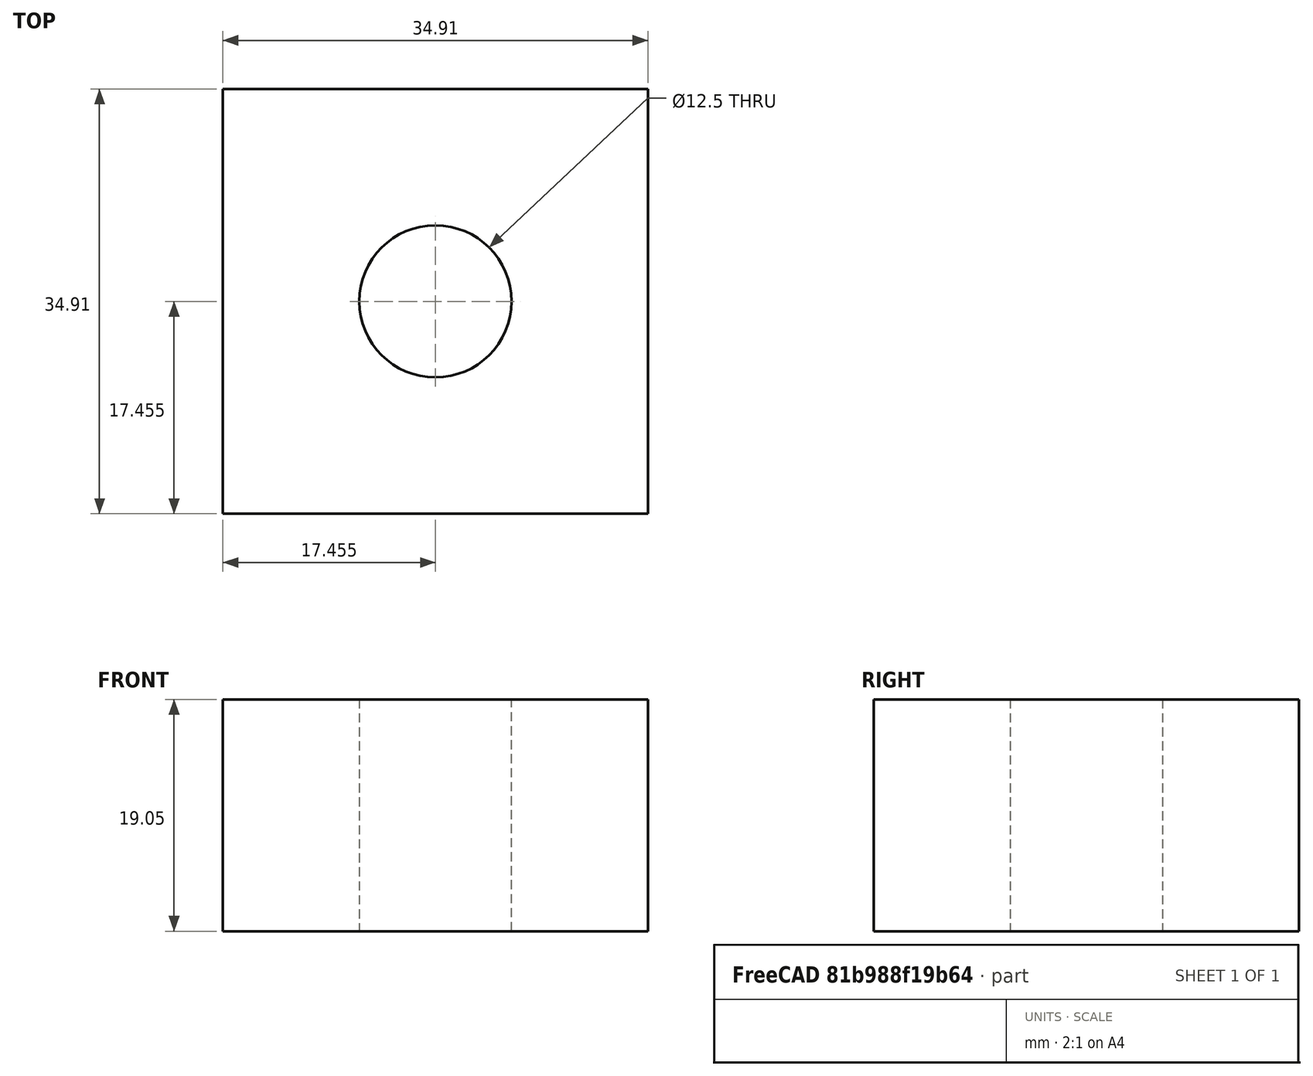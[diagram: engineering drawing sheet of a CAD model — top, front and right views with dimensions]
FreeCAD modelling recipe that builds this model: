
FCSTD DOCUMENT  (FreeCAD 0.19R24291 (Git))
Label: footMountFront
License: All rights reserved
LicenseURL: http://en.wikipedia.org/wiki/All_rights_reserved
objects: Sketcher::SketchObject×1, PartDesign::Pad×1, PartDesign::Body×1
note: 4 computed .brp shape members not serialized (recipe doc carries the construction recipe); baked Part::Feature solids carry a one-line shape summary decoded from their .brp

FEATURE [Sketcher::SketchObject] Sketch
  FullyConstrained = false
  MapMode = 5
  Support = -> [XY_Plane]
  sketch-geometry (24):
    g0: LineSegment StartX=0 StartY=562.08 StartZ=0 EndX=19.08 EndY=562.08 EndZ=0
    g1: LineSegment StartX=19.08 StartY=562.08 StartZ=0 EndX=19.08 EndY=19.08 EndZ=0
    g2: LineSegment StartX=19.08 StartY=19.08 StartZ=0 EndX=0 EndY=19.08 EndZ=0
    g3: LineSegment StartX=0 StartY=19.08 StartZ=0 EndX=0 EndY=562.08 EndZ=0
    g4: LineSegment StartX=0 StartY=0 StartZ=0 EndX=647.65 EndY=0 EndZ=0
    g5: LineSegment StartX=647.65 StartY=0 StartZ=0 EndX=647.65 EndY=19.08 EndZ=0
    g6: LineSegment StartX=647.65 StartY=19.08 StartZ=0 EndX=0 EndY=19.08 EndZ=0
    g7: LineSegment StartX=0 StartY=19.08 StartZ=0 EndX=0 EndY=0 EndZ=0
    g8: LineSegment StartX=628.57 StartY=562.08 StartZ=0 EndX=647.65 EndY=562.08 EndZ=0
    g9: LineSegment StartX=647.65 StartY=562.08 StartZ=0 EndX=647.65 EndY=19.08 EndZ=0
    g10: LineSegment StartX=647.65 StartY=19.08 StartZ=0 EndX=628.57 EndY=19.08 EndZ=0
    g11: LineSegment StartX=628.57 StartY=19.08 StartZ=0 EndX=628.57 EndY=562.08 EndZ=0
    g12: LineSegment StartX=19.08 StartY=19.08 StartZ=0 EndX=53.99 EndY=19.08 EndZ=0
    g13: LineSegment StartX=53.99 StartY=19.08 StartZ=0 EndX=53.99 EndY=53.99 EndZ=0
    g14: LineSegment StartX=53.99 StartY=53.99 StartZ=0 EndX=19.08 EndY=53.99 EndZ=0
    g15: LineSegment StartX=19.08 StartY=53.99 StartZ=0 EndX=19.08 EndY=19.08 EndZ=0
    g16: LineSegment StartX=-141.684 StartY=53.99 StartZ=0 EndX=670.005 EndY=53.99 EndZ=0
    g17: LineSegment StartX=670.005 StartY=53.99 StartZ=0 EndX=670.005 EndY=-34.91 EndZ=0
    g18: LineSegment StartX=670.005 StartY=-34.91 StartZ=0 EndX=-141.684 EndY=-34.91 EndZ=0
    g19: LineSegment StartX=-141.684 StartY=-34.91 StartZ=0 EndX=-141.684 EndY=53.99 EndZ=0
    g20: LineSegment StartX=-141.684 StartY=9.54 StartZ=0 EndX=0 EndY=9.54 EndZ=0
    g21: LineSegment StartX=19.08 StartY=53.99 StartZ=0 EndX=53.99 EndY=19.08 EndZ=0
    g22: LineSegment StartX=53.99 StartY=53.99 StartZ=0 EndX=19.08 EndY=19.08 EndZ=0
    g23: Circle CenterX=36.535 CenterY=36.535 CenterZ=0 NormalX=0 NormalY=0 NormalZ=1 AngleXU=0 Radius=6.25
  constraints (64):
    c: Coincident(g0,g1)
    c: Coincident(g1,g2)
    c: Coincident(g2,g3)
    c: Coincident(g3,g0)
    c: Horizontal(g0)
    c: Horizontal(g2)
    c: Vertical(g1)
    c: Vertical(g3)
    c: DistanceX(g2,g2) = 19.08
    c: DistanceY(g3,g3) = 543
    c: Coincident(g4,g5)
    c: Coincident(g5,g6)
    c: Coincident(g6,g7)
    c: Coincident(g7,g4)
    c: Horizontal(g4)
    c: Horizontal(g6)
    c: Vertical(g5)
    c: Vertical(g7)
    c: Equal(g7,g2)
    c: Coincident(g4,g-1)
    c: Coincident(g2,g6)
    c: DistanceX(g4,g4) = 647.65
    c: Coincident(g8,g9)
    c: Coincident(g9,g10)
    c: Coincident(g10,g11)
    c: Coincident(g11,g8)
    c: Horizontal(g8)
    c: Horizontal(g10)
    c: Vertical(g9)
    c: Vertical(g11)
    c: Equal(g8,g0)
    c: Equal(g11,g1)
    c: Coincident(g9,g5)
    c: Coincident(g12,g13)
    c: Coincident(g13,g14)
    c: Coincident(g14,g15)
    c: Coincident(g15,g12)
    c: Horizontal(g12)
    c: Horizontal(g14)
    c: Vertical(g13)
    c: Vertical(g15)
    c: Coincident(g12,g1)
    c: Coincident(g16,g17)
    c: Coincident(g17,g18)
    c: Coincident(g18,g19)
    c: Coincident(g19,g16)
    c: Horizontal(g16)
    c: Horizontal(g18)
    c: Vertical(g17)
    c: Vertical(g19)
    c: Symmetric(g2,g-1,g20)
    c: Parallel(g20,g4)
    c: Symmetric(g18,g16,g20)
    c: DistanceY(g19,g19) = 88.9
    c: PointOnObject(g13,g16)
    c: DistanceY(g13,g13) = 34.91
    c: Equal(g14,g13)
    c: Coincident(g21,g14)
    c: Coincident(g22,g12)
    c: Coincident(g22,g13)
    c: Coincident(g21,g12)
    c: PointOnObject(g23,g21)
    c: PointOnObject(g23,g22)
    c: Radius(g23) = 6.25
FEATURE [PartDesign::Pad] Pad
  Direction = (1,1,1)
  Length = 19.05
  Length2 = 100
  Profile = -> Sketch
  Type = 0
  expr: Length = 3 / 4 * 25.4
FEATURE [PartDesign::Body] Body
  Group = -> [Sketch,Pad]
  Origin = -> Origin
  Tip = -> Pad
